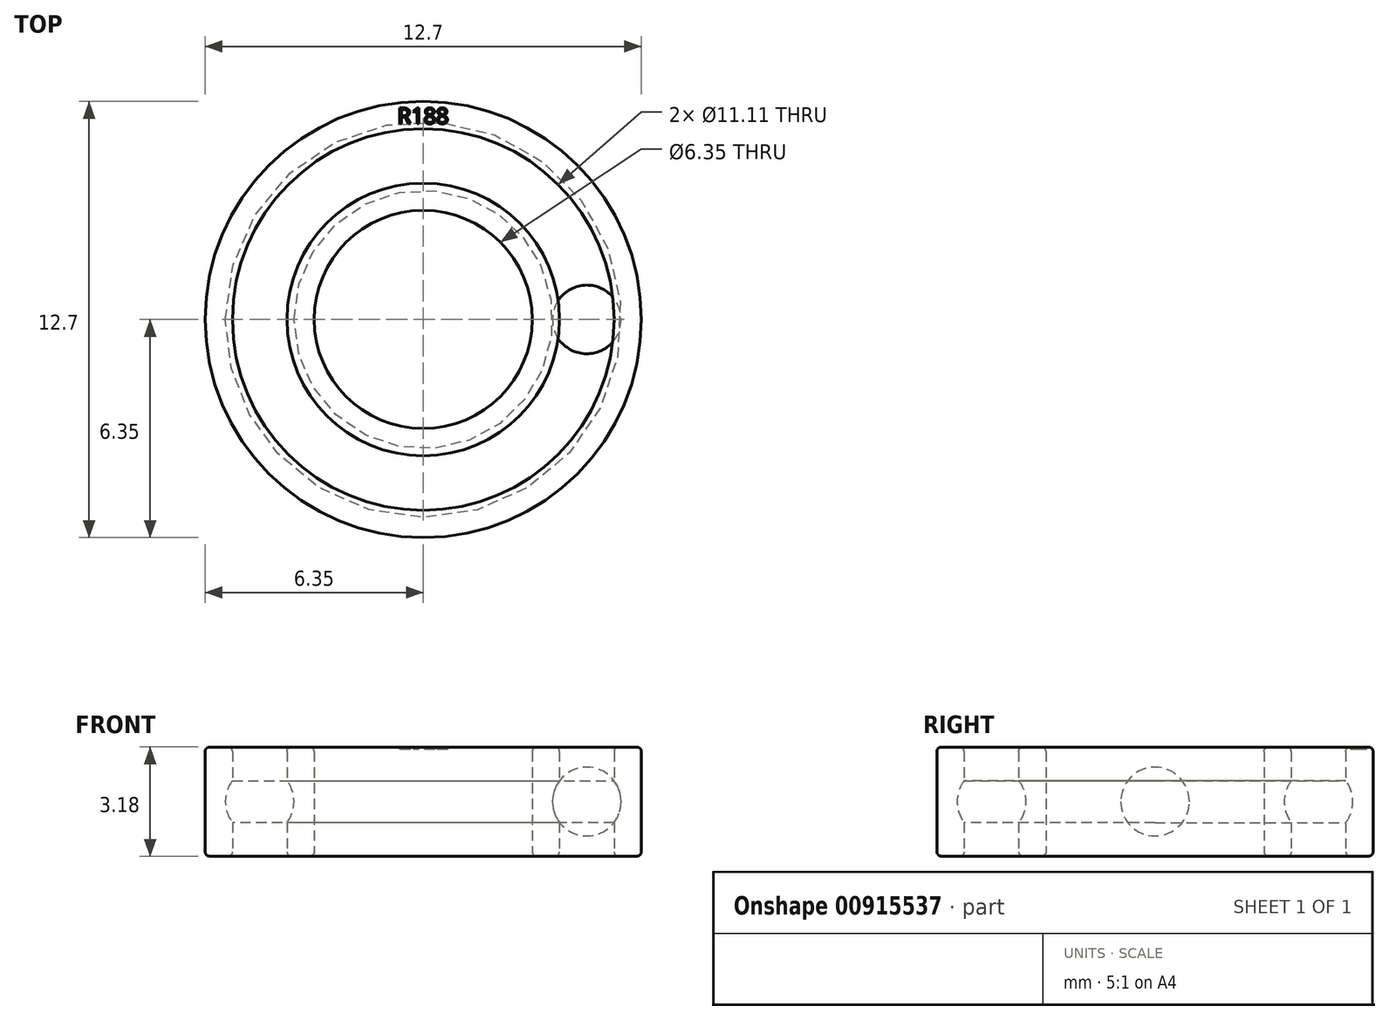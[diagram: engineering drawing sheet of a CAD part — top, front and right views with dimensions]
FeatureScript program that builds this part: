
annotation { "Feature Type Name" : "Feature", "Feature Type Description" : "" }
export const myFeature = defineFeature(function(context is Context, id is Id, definition is map)
    precondition{}
    {
        {
            var Q0;
            Q0=qCreatedBy(makeId("Top.planeOp"),FACE);
            var sketch = newSketch(context, id + "F0", { "sketchPlane" : qUnion([Q0])});
            skCircle(sketch, "E0", {"center": v(0, 0) * mm, "radius": 6.35 * mm});
            skCircle(sketch, "E1", {"center": v(0, 0) * mm, "radius": 5.56 * mm});
            skSolve(sketch);
        }
        {
            var Q0;
            Q0=qCreatedBy(makeId("Top.planeOp"),FACE);
            var sketch = newSketch(context, id + "F1", { "sketchPlane" : qUnion([Q0])});
            skCircle(sketch, "E2", {"center": v(0, 0) * mm, "radius": 3.18 * mm});
            skCircle(sketch, "E3", {"center": v(0, 0) * mm, "radius": 3.97 * mm});
            skSolve(sketch);
        }
        {
            var Q0;
            Q0 = qSketchRegion(id + "F0", true);
            extrude(context, id + "F2", {"entities" : qUnion([Q0]), "endBound" : BoundingType.SYMMETRIC, "depth" : 3.17 * mm, "offsetDistance" : 25.4 * mm});
        }
        {
            var Q0;
            Q0 = qSketchRegion(id + "F1", true);
            extrude(context, id + "F3", {"entities" : qUnion([Q0]), "endBound" : BoundingType.SYMMETRIC, "depth" : 3.17 * mm, "offsetDistance" : 25.4 * mm});
        }
        {
            var Q0;
            Q0=makeQuery(id+"F2.opExtrude","CAP_EDGE",EDGE,{"disambiguationData":[OSD([sQuery(id+"F0.wireOp",EDGE,"E0")])],"isStart":false});
            var Q1;
            Q1=makeQuery(id+"F3.opExtrude","CAP_EDGE",EDGE,{"disambiguationData":[OSD([sQuery(id+"F1.wireOp",EDGE,"E2")])],"isStart":false});
            var Q2;
            Q2=makeQuery(id+"F2.opExtrude","CAP_EDGE",EDGE,{"disambiguationData":[OSD([sQuery(id+"F0.wireOp",EDGE,"E0")])],"isStart":true});
            var Q3;
            Q3=makeQuery(id+"F3.opExtrude","CAP_EDGE",EDGE,{"disambiguationData":[OSD([sQuery(id+"F1.wireOp",EDGE,"E2")])],"isStart":true});
            var Q4;
            Q4=makeQuery(id+"F2.opExtrude","CAP_EDGE",EDGE,{"disambiguationData":[OSD([sQuery(id+"F0.wireOp",EDGE,"E1")])],"isStart":false});
            var Q5;
            Q5=makeQuery(id+"F3.opExtrude","CAP_EDGE",EDGE,{"disambiguationData":[OSD([sQuery(id+"F1.wireOp",EDGE,"E3")])],"isStart":false});
            var Q6;
            Q6=makeQuery(id+"F3.opExtrude","CAP_EDGE",EDGE,{"disambiguationData":[OSD([sQuery(id+"F1.wireOp",EDGE,"E3")])],"isStart":true});
            var Q7;
            Q7=makeQuery(id+"F2.opExtrude","CAP_EDGE",EDGE,{"disambiguationData":[OSD([sQuery(id+"F0.wireOp",EDGE,"E1")])],"isStart":true});
            fillet(context, id + "F4", {"entities" : qUnion([Q0, Q1, Q2, Q3, Q4, Q5, Q6, Q7]), "radius" : 0.13 * mm, "tangentPropagation" : true, "allowEdgeOverflow" : false});
        }
        {
            var Q0;
            Q0=qCreatedBy(makeId("Front.planeOp"),FACE);
            var sketch = newSketch(context, id + "F5", { "sketchPlane" : qUnion([Q0])});
            skCircle(sketch, "E4", {"center": v(4.76, 0) * mm, "radius": 1 * mm});
            skSolve(sketch);
        }
        {
            var Q0;
            Q0 = qSketchRegion(id + "F5", true);
            var Q1;
            Q1=makeQuery(id+"F2.opExtrude","SWEPT_FACE",FACE,{"disambiguationData":[OSD([sQuery(id+"F0.wireOp",EDGE,"E0")])]});
            revolve(context, id + "F6", {"operationType" : NewBodyOperationType.REMOVE, "surfaceOperationType" : NewSurfaceOperationType.NEW, "entities" : qUnion([Q0]), "axis" : qUnion([Q1]), "revolveType" : RevolveType.FULL, "oppositeDirection" : true});
        }
        {
            var Q0;
            Q0=qCreatedBy(makeId("Top.planeOp"),FACE);
            var sketch = newSketch(context, id + "F7", { "sketchPlane" : qUnion([Q0])});
            skArc(sketch, "E5", {"start": v(4.76, -1) * mm, "mid": v(5.76, 0) * mm, "end": v(4.76, 1) * mm});
            skLineSegment(sketch, "E6", {"start": v(4.76, 1) * mm, "end": v(4.76, -1) * mm});
            skSolve(sketch);
        }
        {
            var Q0;
            Q0 = qSketchRegion(id + "F7", true);
            var Q1;
            Q1=sQuery(id+"F7.wireOp",EDGE,"E6");
            revolve(context, id + "F8", {"surfaceOperationType" : NewSurfaceOperationType.NEW, "entities" : qUnion([Q0]), "axis" : qUnion([Q1]), "revolveType" : RevolveType.FULL});
        }
        {
            var Q0;
            Q0=makeQuery(id+"F2.opExtrude","CAP_FACE",FACE,{"disambiguationData":[OSD([sQuery(id+"F0.wireOp",EDGE,"E0"),sQuery(id+"F0.wireOp",EDGE,"E1")])],"isStart":false});
            var sketch = newSketch(context, id + "F9", { "sketchPlane" : qUnion([Q0])});
            skText(sketch, "E7", { "text": "R188", "fontName": "OpenSans-Regular.ttf"});
            const initialGuessF9  = {"E7": [-0.00075, 0.0057, 1, 0, 0.00046]};
            skSetInitialGuess(sketch, initialGuessF9);
            skSolve(sketch);
        }
        {
            var Q0;
            Q0=makeQuery(id+"F9.imprint","IMPRINT",FACE,{"disambiguationData":[TD([[makeQuery(id+"F9.imprint","IMPRINT",EDGE,{"derivedFrom":sQuery(id+"F9.wireOp",EDGE,"E7.sketch_text.stroke-0")}),-1.0]])]});
            var Q1;
            Q1=makeQuery(id+"F9.imprint","IMPRINT",FACE,{"disambiguationData":[TD([[makeQuery(id+"F9.imprint","IMPRINT",EDGE,{"derivedFrom":sQuery(id+"F9.wireOp",EDGE,"E7.sketch_text.stroke-18")}),-1.0]])]});
            var Q2;
            Q2=makeQuery(id+"F9.imprint","IMPRINT",FACE,{"disambiguationData":[TD([[makeQuery(id+"F9.imprint","IMPRINT",EDGE,{"derivedFrom":sQuery(id+"F9.wireOp",EDGE,"E7.sketch_text.stroke-27")}),-1.0]])]});
            var Q3;
            Q3=makeQuery(id+"F9.imprint","IMPRINT",FACE,{"disambiguationData":[TD([[makeQuery(id+"F9.imprint","IMPRINT",EDGE,{"derivedFrom":sQuery(id+"F9.wireOp",EDGE,"E7.sketch_text.stroke-58")}),-1.0]])]});
            extrude(context, id + "F10", {"entities" : qUnion([Q0, Q1, Q2, Q3]), "operationType" : NewBodyOperationType.REMOVE, "oppositeDirection" : true, "depth" : 0.05 * mm, "offsetDistance" : 25.4 * mm});
        }
    });
